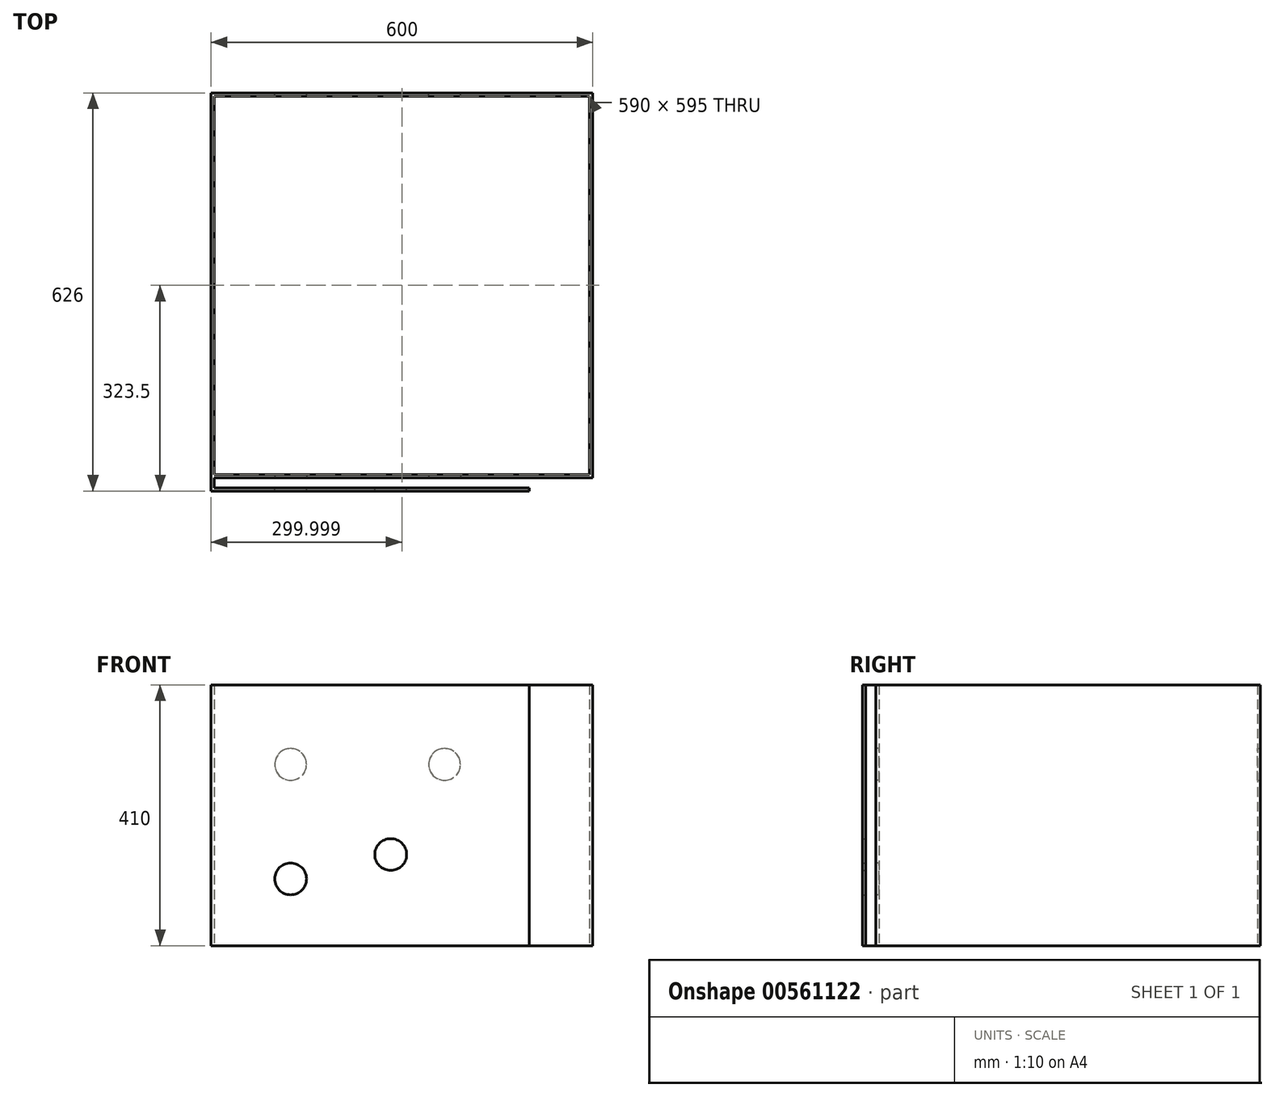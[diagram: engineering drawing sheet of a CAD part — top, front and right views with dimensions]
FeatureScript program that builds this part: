
annotation { "Feature Type Name" : "Feature", "Feature Type Description" : "" }
export const myFeature = defineFeature(function(context is Context, id is Id, definition is map)
    precondition{}
    {
        {
            var Q0;
            Q0=qCreatedBy(makeId("Front.planeOp"),FACE);
            var sketch = newSketch(context, id + "F0", { "sketchPlane" : qUnion([Q0])});
            skLineSegment(sketch, "E0.bottom", {"start": v(-123.13, -99.56) * mm, "end": v(476.87, -99.56) * mm});
            skLineSegment(sketch, "E0.top", {"start": v(-123.13, 310.44) * mm, "end": v(476.87, 310.44) * mm});
            skLineSegment(sketch, "E0.left", {"start": v(-123.13, -99.56) * mm, "end": v(-123.13, 310.44) * mm});
            skLineSegment(sketch, "E0.right", {"start": v(476.87, -99.56) * mm, "end": v(476.87, 310.44) * mm});
            skSolve(sketch);
        }
        {
            var Q0;
            Q0 = qSketchRegion(id + "F0", true);
            extrude(context, id + "F1", {"entities" : qUnion([Q0]), "depth" : 5 * mm, "offsetDistance" : 25.4 * mm});
        }
        {
            var Q0;
            Q0=makeQuery(id+"F1.opExtrude","CAP_FACE",FACE,{"disambiguationData":[OSD([sQuery(id+"F0.wireOp",EDGE,"E0.bottom"),sQuery(id+"F0.wireOp",EDGE,"E0.top"),sQuery(id+"F0.wireOp",EDGE,"E0.left"),sQuery(id+"F0.wireOp",EDGE,"E0.right")])],"isStart":false});
            var sketch = newSketch(context, id + "F2", { "sketchPlane" : qUnion([Q0])});
            skPoint(sketch, "E1", {"position": v(1.87, 185.44) * mm});
            skPoint(sketch, "E2", {"position": v(1.87, 5.44) * mm});
            skPoint(sketch, "E3", {"position": v(243.87, 185.44) * mm});
            skPoint(sketch, "E4", {"position": v(159.27, 43.78) * mm});
            skCircle(sketch, "E5", {"center": v(1.87, 185.44) * mm, "radius": 25 * mm});
            skCircle(sketch, "E6", {"center": v(243.87, 185.44) * mm, "radius": 25 * mm});
            skCircle(sketch, "E7", {"center": v(1.87, 5.44) * mm, "radius": 25 * mm});
            skCircle(sketch, "E8", {"center": v(159.27, 43.78) * mm, "radius": 25 * mm});
            skLineSegment(sketch, "E9.bottom", {"start": v(-123.13, 310.44) * mm, "end": v(-118.13, 310.44) * mm});
            skLineSegment(sketch, "E9.top", {"start": v(-123.13, -99.56) * mm, "end": v(-118.13, -99.56) * mm});
            skLineSegment(sketch, "E9.left", {"start": v(-123.13, 310.44) * mm, "end": v(-123.13, -99.56) * mm});
            skLineSegment(sketch, "E9.right", {"start": v(-118.13, 310.44) * mm, "end": v(-118.13, -99.56) * mm});
            skSolve(sketch);
        }
        {
            var Q0;
            Q0=makeQuery(id+"F1.opExtrude","CAP_FACE",FACE,{"disambiguationData":[OSD([sQuery(id+"F0.wireOp",EDGE,"E0.bottom"),sQuery(id+"F0.wireOp",EDGE,"E0.top"),sQuery(id+"F0.wireOp",EDGE,"E0.left"),sQuery(id+"F0.wireOp",EDGE,"E0.right")])],"isStart":true});
            var sketch = newSketch(context, id + "F3", { "sketchPlane" : qUnion([Q0])});
            skLineSegment(sketch, "E10.bottom", {"start": v(-476.87, 310.44) * mm, "end": v(-471.87, 310.44) * mm});
            skLineSegment(sketch, "E10.top", {"start": v(-476.87, -99.56) * mm, "end": v(-471.87, -99.56) * mm});
            skLineSegment(sketch, "E10.left", {"start": v(-476.87, 310.44) * mm, "end": v(-476.87, -99.56) * mm});
            skLineSegment(sketch, "E10.right", {"start": v(-471.87, 310.44) * mm, "end": v(-471.87, -99.56) * mm});
            skLineSegment(sketch, "E11.bottom", {"start": v(123.13, 310.44) * mm, "end": v(118.13, 310.44) * mm});
            skLineSegment(sketch, "E11.top", {"start": v(123.13, -99.56) * mm, "end": v(118.13, -99.56) * mm});
            skLineSegment(sketch, "E11.left", {"start": v(123.13, 310.44) * mm, "end": v(123.13, -99.56) * mm});
            skLineSegment(sketch, "E11.right", {"start": v(118.13, 310.44) * mm, "end": v(118.13, -99.56) * mm});
            skSolve(sketch);
        }
        {
            var Q0;
            Q0 = qSketchRegion(id + "F3", true);
            extrude(context, id + "F4", {"entities" : qUnion([Q0]), "operationType" : NewBodyOperationType.ADD, "depth" : 600 * mm, "offsetDistance" : 25.4 * mm});
        }
        {
            var Q0;
            Q0=makeQuery(id+"F4.opExtrude","SWEPT_FACE",FACE,{"disambiguationData":[OSD([sQuery(id+"F3.wireOp",EDGE,"E10.right")])]});
            var sketch = newSketch(context, id + "F5", { "sketchPlane" : qUnion([Q0])});
            skLineSegment(sketch, "E12.bottom", {"start": v(-600, 310.44) * mm, "end": v(-595, 310.44) * mm});
            skLineSegment(sketch, "E12.top", {"start": v(-600, -99.56) * mm, "end": v(-595, -99.56) * mm});
            skLineSegment(sketch, "E12.left", {"start": v(-600, 310.44) * mm, "end": v(-600, -99.56) * mm});
            skLineSegment(sketch, "E12.right", {"start": v(-595, 310.44) * mm, "end": v(-595, -99.56) * mm});
            skSolve(sketch);
        }
        {
            var Q0;
            Q0 = qSketchRegion(id + "F5", true);
            extrude(context, id + "F6", {"entities" : qUnion([Q0]), "operationType" : NewBodyOperationType.ADD, "depth" : 591 * mm, "offsetDistance" : 25.4 * mm});
        }
        {
            var Q0;
            Q0=makeQuery(id+"F6.boolean.opBoolean","MERGE",FACE,{"derivedFrom":[makeQuery(id+"F4.opExtrude","CAP_FACE",FACE,{"disambiguationData":[OSD([sQuery(id+"F3.wireOp",EDGE,"E10.bottom"),sQuery(id+"F3.wireOp",EDGE,"E10.top"),sQuery(id+"F3.wireOp",EDGE,"E10.left"),sQuery(id+"F3.wireOp",EDGE,"E10.right")])],"isStart":false}),makeQuery(id+"F4.opExtrude","CAP_FACE",FACE,{"disambiguationData":[OSD([sQuery(id+"F3.wireOp",EDGE,"E11.bottom"),sQuery(id+"F3.wireOp",EDGE,"E11.top"),sQuery(id+"F3.wireOp",EDGE,"E11.left"),sQuery(id+"F3.wireOp",EDGE,"E11.right")])],"isStart":false}),makeQuery(id+"F6.opExtrude","SWEPT_FACE",FACE,{"disambiguationData":[OSD([sQuery(id+"F5.wireOp",EDGE,"E12.left")])]})]});
            var sketch = newSketch(context, id + "F7", { "sketchPlane" : qUnion([Q0])});
            skPoint(sketch, "E13", {"position": v(-1.87, 185.44) * mm});
            skCircle(sketch, "E14", {"center": v(-1.87, 185.44) * mm, "radius": 25 * mm});
            skPoint(sketch, "E15", {"position": v(-243.87, 185.44) * mm});
            skCircle(sketch, "E16", {"center": v(-243.87, 185.44) * mm, "radius": 25 * mm});
            skSolve(sketch);
        }
        {
            var Q0;
            Q0 = qSketchRegion(id + "F7", true);
            extrude(context, id + "F8", {"entities" : qUnion([Q0]), "operationType" : NewBodyOperationType.REMOVE, "oppositeDirection" : true, "depth" : 25.4 * mm, "offsetDistance" : 25.4 * mm});
        }
        {
            var Q0;
            Q0=makeQuery(id+"F2.imprint","IMPRINT",FACE,{"disambiguationData":[TD([[makeQuery(id+"F2.imprint","IMPRINT",EDGE,{"derivedFrom":sQuery(id+"F2.wireOp",EDGE,"E5")}),1.0]])]});
            extrude(context, id + "F9", {"entities" : qUnion([Q0]), "operationType" : NewBodyOperationType.REMOVE, "oppositeDirection" : true, "depth" : 25.4 * mm, "offsetDistance" : 25.4 * mm});
        }
        {
            var Q0;
            Q0=makeQuery(id+"F2.imprint","IMPRINT",FACE,{"disambiguationData":[TD([[makeQuery(id+"F2.imprint","IMPRINT",EDGE,{"derivedFrom":sQuery(id+"F2.wireOp",EDGE,"E6")}),1.0]])]});
            extrude(context, id + "F10", {"entities" : qUnion([Q0]), "operationType" : NewBodyOperationType.REMOVE, "oppositeDirection" : true, "depth" : 25.4 * mm, "offsetDistance" : 25.4 * mm});
        }
        {
            var Q0;
            Q0=makeQuery(id+"F2.imprint","IMPRINT",FACE,{"disambiguationData":[TD([[makeQuery(id+"F2.imprint","IMPRINT",EDGE,{"derivedFrom":sQuery(id+"F2.wireOp",EDGE,"E7")}),1.0]])]});
            extrude(context, id + "F11", {"entities" : qUnion([Q0]), "operationType" : NewBodyOperationType.REMOVE, "oppositeDirection" : true, "depth" : 25.4 * mm, "offsetDistance" : 25.4 * mm});
        }
        {
            var Q0;
            Q0=makeQuery(id+"F2.imprint","IMPRINT",FACE,{"disambiguationData":[TD([[makeQuery(id+"F2.imprint","IMPRINT",EDGE,{"derivedFrom":sQuery(id+"F2.wireOp",EDGE,"E9.bottom")}),-1.0]])]});
            extrude(context, id + "F12", {"entities" : qUnion([Q0]), "operationType" : NewBodyOperationType.ADD, "depth" : 21 * mm, "offsetDistance" : 25.4 * mm});
        }
        {
            var Q0;
            Q0=makeQuery(id+"F12.opExtrude","SWEPT_FACE",FACE,{"disambiguationData":[OSD([sQuery(id+"F2.wireOp",EDGE,"E9.right")])]});
            var sketch = newSketch(context, id + "F13", { "sketchPlane" : qUnion([Q0])});
            skLineSegment(sketch, "E17.bottom", {"start": v(-26, 310.44) * mm, "end": v(-21, 310.44) * mm});
            skLineSegment(sketch, "E17.top", {"start": v(-26, -99.56) * mm, "end": v(-21, -99.56) * mm});
            skLineSegment(sketch, "E17.left", {"start": v(-26, 310.44) * mm, "end": v(-26, -99.56) * mm});
            skLineSegment(sketch, "E17.right", {"start": v(-21, 310.44) * mm, "end": v(-21, -99.56) * mm});
            skSolve(sketch);
        }
        {
            var Q0;
            Q0 = qSketchRegion(id + "F13", true);
            extrude(context, id + "F14", {"entities" : qUnion([Q0]), "operationType" : NewBodyOperationType.ADD, "depth" : 495 * mm, "offsetDistance" : 25.4 * mm});
        }
        {
            var Q0;
            Q0=makeQuery(id+"F2.imprint","IMPRINT",FACE,{"disambiguationData":[TD([[makeQuery(id+"F2.imprint","IMPRINT",EDGE,{"derivedFrom":sQuery(id+"F2.wireOp",EDGE,"E7")}),1.0]])]});
            extrude(context, id + "F15", {"entities" : qUnion([Q0]), "operationType" : NewBodyOperationType.REMOVE, "depth" : 76.2 * mm, "offsetDistance" : 25.4 * mm});
        }
        {
            var Q0;
            Q0=makeQuery(id+"F2.imprint","IMPRINT",FACE,{"disambiguationData":[TD([[makeQuery(id+"F2.imprint","IMPRINT",EDGE,{"derivedFrom":sQuery(id+"F2.wireOp",EDGE,"E8")}),1.0]])]});
            var Q1;
            Q1=sQuery(id+"F2.wireOp",EDGE,"E8");
            extrude(context, id + "F16", {"entities" : qUnion([Q0]), "operationType" : NewBodyOperationType.REMOVE, "surfaceEntities" : qUnion([Q1]), "depth" : 25.4 * mm, "offsetDistance" : 25.4 * mm});
        }
    });
